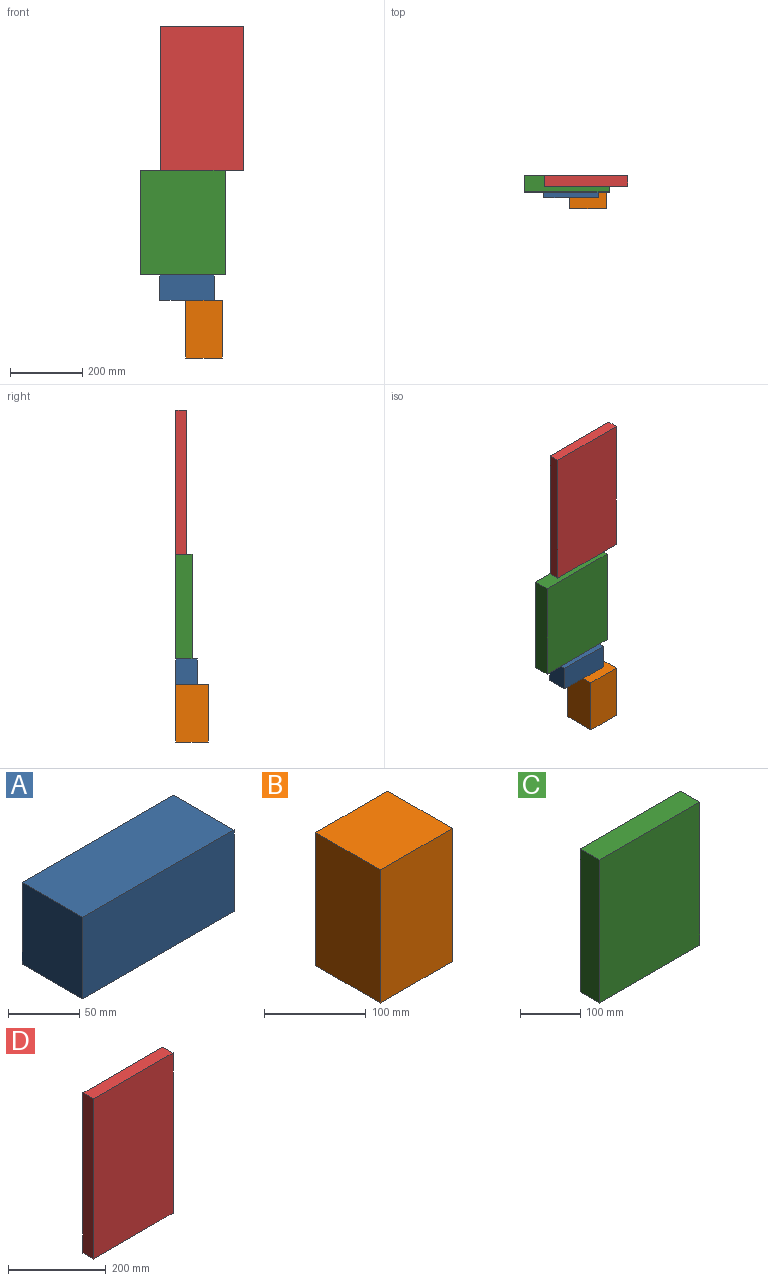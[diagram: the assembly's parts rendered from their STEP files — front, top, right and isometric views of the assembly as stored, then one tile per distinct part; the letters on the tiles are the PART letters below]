
ASSEMBLY  parts=4 mates=6
PART A: 6 faces, bbox 150x60x70 mm
  f0: plane 70x60mm, normal (-1,0,0), area 4200mm2, adj f1,f3,f4,f5
  f1: plane 150x60mm, normal (0,0,-1), area 9000mm2, adj f0,f2,f4,f5
  f2: plane 70x60mm, normal (1,0,0), area 4200mm2, adj f1,f3,f4,f5
  f3: plane 150x60mm, normal (0,0,1), area 9000mm2, adj f0,f2,f4,f5
  f4: plane 150x70mm, normal (0,-1,0), area 10500mm2, adj f0,f1,f2,f3
  f5: plane 150x70mm, normal (0,1,0), area 10500mm2, adj f0,f1,f2,f3
PART B: 11 faces, bbox 100x90x160 mm
  f0: plane 160x90mm, normal (1,0,0), area 4600mm2, adj f2,f3,f4,f5,f7,f8,f9,f10
  f1: plane 160x90mm, normal (-1,0,0), area 14400mm2, adj f2,f3,f4,f5
  f2: plane 100x90mm, normal (0,0,-1), area 9000mm2, adj f0,f1,f4,f5
  f3: plane 100x90mm, normal (0,0,1), area 9000mm2, adj f0,f1,f4,f5
  f4: plane 160x100mm, normal (0,-1,0), area 16000mm2, adj f0,f1,f2,f3
  f5: plane 160x100mm, normal (0,1,0), area 16000mm2, adj f0,f1,f2,f3
  f6: plane 140x70mm, normal (1,0,0), area 9800mm2, adj f7,f8,f9,f10
  f7: plane 90x70mm, normal (0,0,1), area 6300mm2, adj f0,f6,f9,f10
  f8: plane 90x70mm, normal (0,0,-1), area 6300mm2, adj f0,f6,f9,f10
  f9: plane 140x90mm, normal (0,1,0), area 12600mm2, adj f0,f6,f7,f8
  f10: plane 140x90mm, normal (0,-1,0), area 12600mm2, adj f0,f6,f7,f8
PART C: 6 faces, bbox 235x45x290 mm
  f0: plane 290x45mm, normal (-1,0,0), area 13050mm2, adj f1,f3,f4,f5
  f1: plane 235x45mm, normal (0,0,-1), area 10575mm2, adj f0,f2,f4,f5
  f2: plane 290x45mm, normal (1,0,0), area 13050mm2, adj f1,f3,f4,f5
  f3: plane 235x45mm, normal (0,0,1), area 10575mm2, adj f0,f2,f4,f5
  f4: plane 290x235mm, normal (0,-1,0), area 68150mm2, adj f0,f1,f2,f3
  f5: plane 290x235mm, normal (0,1,0), area 68150mm2, adj f0,f1,f2,f3
PART D: 6 faces, bbox 230x30x400 mm
  f0: plane 400x30mm, normal (-1,0,0), area 12000mm2, adj f1,f3,f4,f5
  f1: plane 230x30mm, normal (0,0,-1), area 6900mm2, adj f0,f2,f4,f5
  f2: plane 400x30mm, normal (1,0,0), area 12000mm2, adj f1,f3,f4,f5
  f3: plane 230x30mm, normal (0,0,1), area 6900mm2, adj f0,f2,f4,f5
  f4: plane 400x230mm, normal (0,-1,0), area 92000mm2, adj f0,f1,f2,f3
  f5: plane 400x230mm, normal (0,1,0), area 92000mm2, adj f0,f1,f2,f3
PLACE A t=(-8.92,-227.61,-526.67)mm
PLACE B t=(63.08,-227.61,-686.67)mm
PLACE C t=(-63.42,-227.61,-456.67)mm
PLACE D t=(-6.93,-227.61,-166.67)mm
MATE planar A.f1 <-> B.f3  axis (0,0,-1) through (66.08,-257.61,-526.67)mm
MATE planar C.f5 <-> A.f5  axis (0,1,0) through (54.08,-227.61,-311.67)mm
MATE planar A.f5 <-> B.f5  axis (0,1,0) through (66.08,-227.61,-491.67)mm
MATE planar C.f3 <-> D.f1  axis (0,0,1) through (54.08,-250.11,-166.67)mm
MATE planar C.f1 <-> A.f3  axis (0,0,-1) through (54.08,-250.11,-456.67)mm
MATE planar D.f5 <-> C.f5  axis (0,1,0) through (108.07,-227.61,33.33)mm
